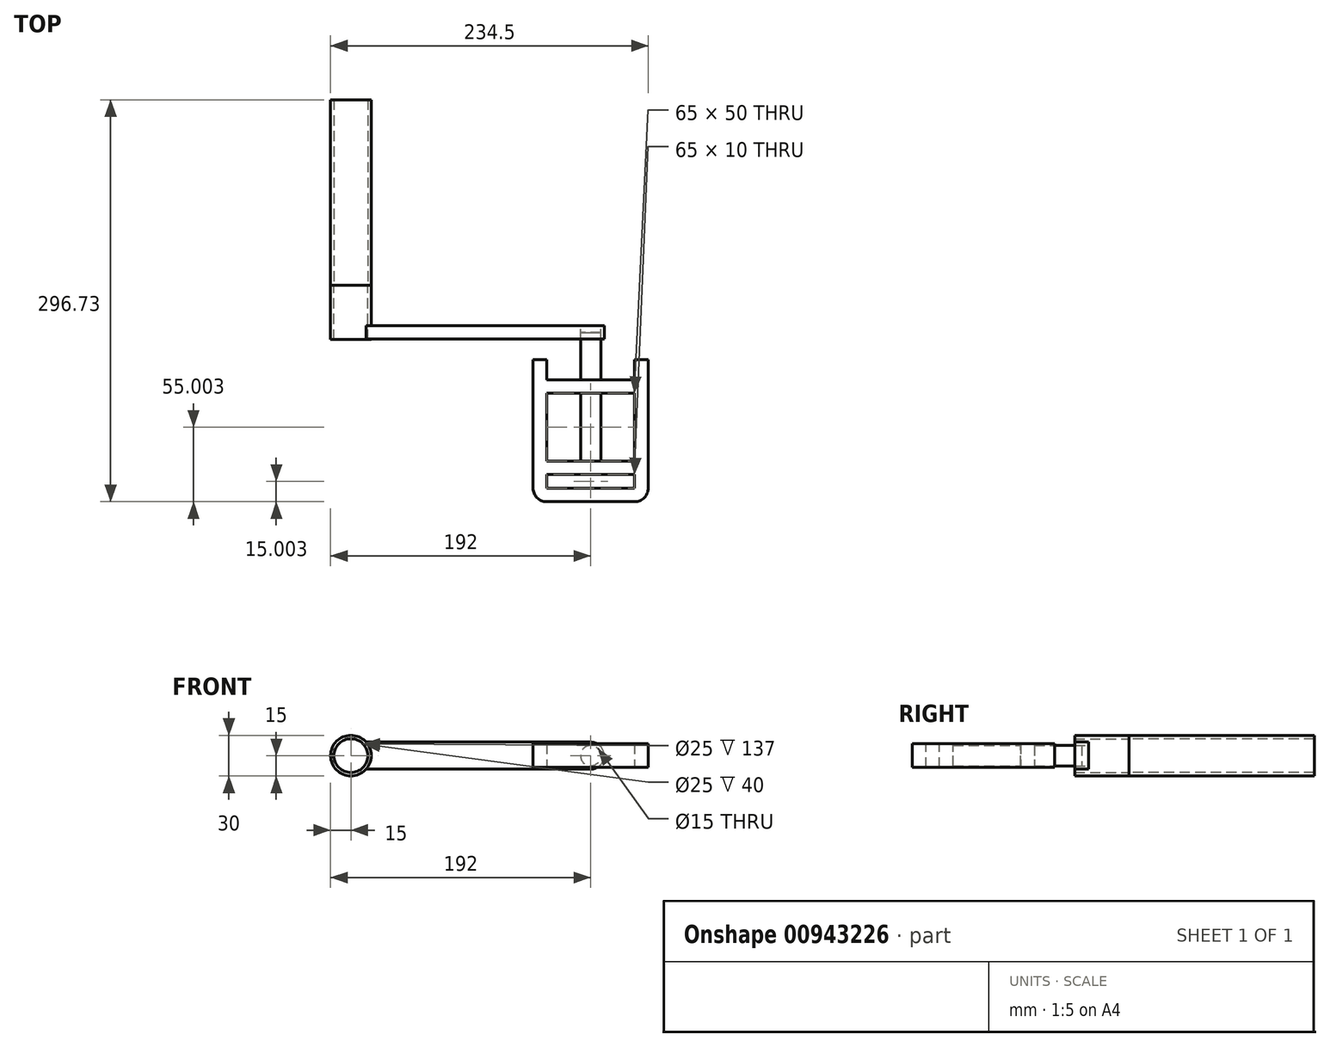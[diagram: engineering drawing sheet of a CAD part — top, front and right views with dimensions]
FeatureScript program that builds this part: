
annotation { "Feature Type Name" : "Feature", "Feature Type Description" : "" }
export const myFeature = defineFeature(function(context is Context, id is Id, definition is map)
    precondition{}
    {
        {
            var Q0;
            Q0=qCreatedBy(makeId("Front.planeOp"),FACE);
            var sketch = newSketch(context, id + "F0", { "sketchPlane" : qUnion([Q0])});
            skCircle(sketch, "E0", {"center": v(0, 0) * mm, "radius": 15 * mm});
            skCircle(sketch, "E1", {"center": v(0, 0) * mm, "radius": 12.5 * mm});
            skSolve(sketch);
        }
        {
            var Q0;
            Q0=makeQuery(id+"F0.imprint","IMPRINT",FACE,{"disambiguationData":[TD([[makeQuery(id+"F0.imprint","IMPRINT",EDGE,{"derivedFrom":sQuery(id+"F0.wireOp",EDGE,"E0")}),1.0]])]});
            extrude(context, id + "F1", {"entities" : qUnion([Q0]), "depth" : 40 * mm, "offsetDistance" : 25 * mm});
        }
        {
            var Q0;
            Q0=makeQuery(id+"F1.opExtrude","CAP_FACE",FACE,{"disambiguationData":[OSD([sQuery(id+"F0.wireOp",EDGE,"E0"),sQuery(id+"F0.wireOp",EDGE,"E1")])],"isStart":false});
            var sketch = newSketch(context, id + "F2", { "sketchPlane" : qUnion([Q0])});
            skLineSegment(sketch, "E2", {"start": v(0, 15) * mm, "end": v(0, -15) * mm});
            skSolve(sketch);
        }
        {
            var Q0;
            Q0=qCreatedBy(makeId("Right.planeOp"),FACE);
            var sketch = newSketch(context, id + "F3", { "sketchPlane" : qUnion([Q0])});
            skLineSegment(sketch, "E3", {"start": v(-39.73, 10) * mm, "end": v(-29.73, 10) * mm});
            skLineSegment(sketch, "E4.top", {"start": v(-39.73, -10) * mm, "end": v(-29.73, -10) * mm});
            skLineSegment(sketch, "E4.left", {"start": v(-39.73, 10) * mm, "end": v(-39.73, -10) * mm});
            skLineSegment(sketch, "E4.right", {"start": v(-29.73, 10) * mm, "end": v(-29.73, -10) * mm});
            skSolve(sketch);
        }
        {
            var Q0;
            Q0=qSketchRegion(id+"F3",true);
            extrude(context, id + "F4", {"entities" : qUnion([Q0]), "operationType" : NewBodyOperationType.ADD, "depth" : 177 * mm, "offsetDistance" : 25 * mm});
        }
        {
            var Q0;
            {var subQ0=sQuery(id+"F2.wireOp",EDGE,"E2");var subQ1=makeQuery(id+"F1.opExtrude","CAP_EDGE",EDGE,{"disambiguationData":[OSD([sQuery(id+"F0.wireOp",EDGE,"E1")])],"isStart":false});var subQ2=makeQuery(id+"F2.imprint","INTERSECT",VERTEX,{"disambiguationData":[OD(0.0)],"derivedFrom":[subQ1,subQ0]});Q0=makeQuery(id+"F2.imprint","IMPRINT",FACE,{"disambiguationData":[TD([[makeQuery(id+"F2.imprint","IMPRINT",EDGE,{"disambiguationData":[TD([[subQ2,-1.0]])],"derivedFrom":subQ0}),1.0]])]});}
            extrude(context, id + "F5", {"entities" : qUnion([Q0]), "operationType" : NewBodyOperationType.REMOVE, "oppositeDirection" : true, "depth" : 11 * mm, "offsetDistance" : 25 * mm});
        }
        {
            var Q0;
            {var subQ1=sQuery(id+"F3.wireOp",EDGE,"E4.right");Q0=makeQuery(id+"F4.boolean.opBoolean","SPLIT",FACE,{"disambiguationData":[TD([makeQuery(id+"F1.opExtrude","SWEPT_FACE",FACE,{"disambiguationData":[OSD([sQuery(id+"F0.wireOp",EDGE,"E0")])]})])],"derivedFrom":makeQuery(id+"F4.opExtrude","SWEPT_FACE",FACE,{"disambiguationData":[OSD([subQ1])]})});}
            var sketch = newSketch(context, id + "F6", { "sketchPlane" : qUnion([Q0])});
            skCircle(sketch, "E5", {"center": v(-177, 0) * mm, "radius": 10 * mm});
            skCircle(sketch, "E6", {"center": v(-177, 0) * mm, "radius": 7.5 * mm});
            skSolve(sketch);
        }
        {
            var Q0;
            {var subQ0=sQuery(id+"F6.wireOp",EDGE,"E6");var subQ1=makeQuery(id+"F4.opExtrude","CAP_EDGE",EDGE,{"disambiguationData":[OSD([sQuery(id+"F3.wireOp",EDGE,"E4.right")])],"isStart":false});var subQ2=makeQuery(id+"F6.imprint","INTERSECT",VERTEX,{"disambiguationData":[OD(0.0)],"derivedFrom":[subQ1,subQ0]});Q0=makeQuery(id+"F6.imprint","IMPRINT",FACE,{"disambiguationData":[TD([[makeQuery(id+"F6.imprint","IMPRINT",EDGE,{"disambiguationData":[TD([[subQ2,1.0]])],"derivedFrom":subQ0}),1.0]])]});}
            extrude(context, id + "F7", {"entities" : qUnion([Q0]), "operationType" : NewBodyOperationType.REMOVE, "oppositeDirection" : true, "depth" : 10 * mm, "offsetDistance" : 25 * mm});
        }
        {
            var Q0;
            Q0=qSketchRegion(id+"F6",true);
            extrude(context, id + "F8", {"entities" : qUnion([Q0]), "operationType" : NewBodyOperationType.ADD, "depth" : -10 * mm, "offsetDistance" : 25 * mm});
        }
        {
            var Q0;
            {var subQ1=sQuery(id+"F3.wireOp",EDGE,"E4.left");Q0=makeQuery(id+"F8.boolean.opBoolean","MERGE",FACE,{"derivedFrom":[makeQuery(id+"F4.boolean.opBoolean","SPLIT",FACE,{"disambiguationData":[TD([makeQuery(id+"F1.opExtrude","SWEPT_FACE",FACE,{"disambiguationData":[OSD([sQuery(id+"F0.wireOp",EDGE,"E0")])]})])],"derivedFrom":makeQuery(id+"F4.opExtrude","SWEPT_FACE",FACE,{"disambiguationData":[OSD([subQ1])]})}),makeQuery(id+"F8.opExtrude","CAP_FACE",FACE,{"disambiguationData":[OSD([sQuery(id+"F6.wireOp",EDGE,"E5"),sQuery(id+"F6.wireOp",EDGE,"E6")])],"isStart":false})]});}
            var sketch = newSketch(context, id + "F9", { "sketchPlane" : qUnion([Q0])});
            skCircle(sketch, "E7", {"center": v(177, 0) * mm, "radius": 7.5 * mm});
            skSolve(sketch);
        }
        {
            var Q0;
            Q0=makeQuery(id+"F9.imprint","IMPRINT",FACE,{"disambiguationData":[TD([[makeQuery(id+"F9.imprint","IMPRINT",EDGE,{"derivedFrom":sQuery(id+"F9.wireOp",EDGE,"E7")}),-1.0]])]});
            extrude(context, id + "F10", {"entities" : qUnion([Q0]), "depth" : 30 * mm, "offsetDistance" : 25 * mm, "hasSecondDirection" : true, "secondDirectionOppositeDirection" : true, "secondDirectionDepth" : 5 * mm});
        }
        {
            var Q0;
            Q0=makeQuery(id+"F10.opExtrude","CAP_FACE",FACE,{"disambiguationData":[OSD([sQuery(id+"F9.wireOp",EDGE,"E7")])],"isStart":false});
            var sketch = newSketch(context, id + "F11", { "sketchPlane" : qUnion([Q0])});
            skLineSegment(sketch, "E8.bottom", {"start": v(209.5, 8.75) * mm, "end": v(144.5, 8.75) * mm});
            skLineSegment(sketch, "E8.top", {"start": v(209.5, -8.75) * mm, "end": v(144.5, -8.75) * mm});
            skLineSegment(sketch, "E8.left", {"start": v(209.5, 8.75) * mm, "end": v(209.5, -8.75) * mm});
            skLineSegment(sketch, "E8.right", {"start": v(144.5, 8.75) * mm, "end": v(144.5, -8.75) * mm});
            skPoint(sketch, "E8.middle", {"position": v(177, 0) * mm});
            skSolve(sketch);
        }
        {
            var Q0;
            Q0=makeQuery(id+"F11.imprint","IMPRINT",FACE,{"disambiguationData":[TD([[makeQuery(id+"F11.imprint","IMPRINT",EDGE,{"derivedFrom":makeQuery(id+"F10.opExtrude","CAP_EDGE",EDGE,{"disambiguationData":[OSD([sQuery(id+"F9.wireOp",EDGE,"E7")])],"isStart":false})}),-1.0]])]});
            var Q1;
            Q1=makeQuery(id+"F11.imprint","IMPRINT",FACE,{"disambiguationData":[TD([[makeQuery(id+"F11.imprint","IMPRINT",EDGE,{"derivedFrom":sQuery(id+"F11.wireOp",EDGE,"E8.bottom")}),1.0]])]});
            extrude(context, id + "F12", {"entities" : qUnion([Q0, Q1]), "operationType" : NewBodyOperationType.ADD, "depth" : 10 * mm, "offsetDistance" : 25 * mm});
        }
        {
            var Q0;
            Q0=makeQuery(id+"F12.opExtrude","CAP_FACE",FACE,{"disambiguationData":[OSD([sQuery(id+"F11.wireOp",EDGE,"E8.bottom"),sQuery(id+"F11.wireOp",EDGE,"E8.top"),sQuery(id+"F11.wireOp",EDGE,"E8.left"),sQuery(id+"F11.wireOp",EDGE,"E8.right")])],"isStart":false});
            var sketch = newSketch(context, id + "F13", { "sketchPlane" : qUnion([Q0])});
            skCircle(sketch, "E9", {"center": v(177, 0) * mm, "radius": 7.5 * mm});
            skSolve(sketch);
        }
        {
            var Q0;
            Q0=makeQuery(id+"F13.imprint","IMPRINT",FACE,{"disambiguationData":[TD([[makeQuery(id+"F13.imprint","IMPRINT",EDGE,{"derivedFrom":sQuery(id+"F13.wireOp",EDGE,"E9")}),1.0]])]});
            extrude(context, id + "F14", {"entities" : qUnion([Q0]), "operationType" : NewBodyOperationType.ADD, "depth" : 50 * mm, "offsetDistance" : 25 * mm});
        }
        {
            var Q0;
            Q0=makeQuery(id+"F14.opExtrude","CAP_FACE",FACE,{"disambiguationData":[OSD([sQuery(id+"F13.wireOp",EDGE,"E9")])],"isStart":false});
            var sketch = newSketch(context, id + "F15", { "sketchPlane" : qUnion([Q0])});
            skLineSegment(sketch, "E10.bottom", {"start": v(209.5, -8.75) * mm, "end": v(144.5, -8.75) * mm});
            skLineSegment(sketch, "E10.top", {"start": v(209.5, 8.75) * mm, "end": v(144.5, 8.75) * mm});
            skLineSegment(sketch, "E10.left", {"start": v(209.5, -8.75) * mm, "end": v(209.5, 8.75) * mm});
            skLineSegment(sketch, "E10.right", {"start": v(144.5, -8.75) * mm, "end": v(144.5, 8.75) * mm});
            skPoint(sketch, "E10.middle", {"position": v(177, 0) * mm});
            skSolve(sketch);
        }
        {
            var Q0;
            Q0=makeQuery(id+"F15.imprint","IMPRINT",FACE,{"disambiguationData":[TD([[makeQuery(id+"F15.imprint","IMPRINT",EDGE,{"derivedFrom":sQuery(id+"F15.wireOp",EDGE,"E10.bottom")}),-1.0]])]});
            var Q1;
            Q1=makeQuery(id+"F15.imprint","IMPRINT",FACE,{"disambiguationData":[TD([[makeQuery(id+"F15.imprint","IMPRINT",EDGE,{"derivedFrom":makeQuery(id+"F14.opExtrude","CAP_EDGE",EDGE,{"disambiguationData":[OSD([sQuery(id+"F13.wireOp",EDGE,"E9")])],"isStart":false})}),1.0]])]});
            extrude(context, id + "F16", {"entities" : qUnion([Q0, Q1]), "operationType" : NewBodyOperationType.ADD, "depth" : 10 * mm, "offsetDistance" : 25 * mm});
        }
        {
            var Q0;
            Q0=makeQuery(id+"F12.opExtrude","SWEPT_FACE",FACE,{"disambiguationData":[OSD([sQuery(id+"F11.wireOp",EDGE,"E8.bottom")])]});
            var sketch = newSketch(context, id + "F17", { "sketchPlane" : qUnion([Q0])});
            skLineSegment(sketch, "E11.bottom", {"start": v(144.5, -69.73) * mm, "end": v(134.5, -69.73) * mm});
            skLineSegment(sketch, "E11.top", {"start": v(144.5, -149.73) * mm, "end": v(134.5, -149.73) * mm});
            skLineSegment(sketch, "E11.left", {"start": v(144.5, -69.73) * mm, "end": v(144.5, -149.73) * mm});
            skLineSegment(sketch, "E11.right", {"start": v(134.5, -69.73) * mm, "end": v(134.5, -149.73) * mm});
            skArc(sketch, "E12", {"start": v(134.5, -149.73) * mm, "mid": v(137.43, -156.8) * mm, "end": v(144.5, -159.73) * mm});
            skLineSegment(sketch, "E13.bottom", {"start": v(144.5, -149.73) * mm, "end": v(209.5, -149.73) * mm});
            skLineSegment(sketch, "E13.top", {"start": v(144.5, -159.73) * mm, "end": v(209.5, -159.73) * mm});
            skLineSegment(sketch, "E13.left", {"start": v(144.5, -149.73) * mm, "end": v(144.5, -159.73) * mm});
            skLineSegment(sketch, "E13.right", {"start": v(209.5, -149.73) * mm, "end": v(209.5, -159.73) * mm});
            skArc(sketch, "E14", {"start": v(209.5, -159.73) * mm, "mid": v(216.57, -156.8) * mm, "end": v(219.5, -149.73) * mm});
            skLineSegment(sketch, "E15.bottom", {"start": v(209.5, -149.73) * mm, "end": v(219.5, -149.73) * mm});
            skLineSegment(sketch, "E15.top", {"start": v(209.5, -69.73) * mm, "end": v(219.5, -69.73) * mm});
            skLineSegment(sketch, "E15.left", {"start": v(209.5, -149.73) * mm, "end": v(209.5, -69.73) * mm});
            skLineSegment(sketch, "E15.right", {"start": v(219.5, -149.73) * mm, "end": v(219.5, -69.73) * mm});
            skLineSegment(sketch, "E16.top", {"start": v(144.5, -54.73) * mm, "end": v(134.5, -54.73) * mm});
            skLineSegment(sketch, "E16.left", {"start": v(144.5, -69.73) * mm, "end": v(144.5, -54.73) * mm});
            skLineSegment(sketch, "E16.right", {"start": v(134.5, -69.73) * mm, "end": v(134.5, -54.73) * mm});
            skLineSegment(sketch, "E17.top", {"start": v(209.5, -54.73) * mm, "end": v(219.5, -54.73) * mm});
            skLineSegment(sketch, "E17.left", {"start": v(209.5, -69.73) * mm, "end": v(209.5, -54.73) * mm});
            skLineSegment(sketch, "E17.right", {"start": v(219.5, -69.73) * mm, "end": v(219.5, -54.73) * mm});
            skSolve(sketch);
        }
        {
            var Q0;
            Q0=makeQuery(id+"F17.imprint","IMPRINT",FACE,{"disambiguationData":[TD([[makeQuery(id+"F17.imprint","IMPRINT",EDGE,{"derivedFrom":sQuery(id+"F17.wireOp",EDGE,"E15.top")}),1.0]])]});
            var Q1;
            {var subQ4=sQuery(id+"F17.wireOp",EDGE,"E15.bottom");Q1=makeQuery(id+"F17.imprint","IMPRINT",FACE,{"disambiguationData":[TD([[makeQuery(id+"F17.imprint","IMPRINT",EDGE,{"derivedFrom":subQ4}),1.0]])]});}
            var Q2;
            Q2=makeQuery(id+"F17.imprint","IMPRINT",FACE,{"disambiguationData":[TD([[makeQuery(id+"F17.imprint","IMPRINT",EDGE,{"derivedFrom":sQuery(id+"F17.wireOp",EDGE,"E13.right")}),1.0]])]});
            var Q3;
            Q3=makeQuery(id+"F17.imprint","IMPRINT",FACE,{"disambiguationData":[TD([[makeQuery(id+"F17.imprint","IMPRINT",EDGE,{"derivedFrom":sQuery(id+"F17.wireOp",EDGE,"E13.bottom")}),-1.0]])]});
            var Q4;
            Q4=makeQuery(id+"F17.imprint","IMPRINT",FACE,{"disambiguationData":[TD([[makeQuery(id+"F17.imprint","IMPRINT",EDGE,{"derivedFrom":sQuery(id+"F17.wireOp",EDGE,"E11.top")}),1.0]])]});
            var Q5;
            {var subQ4=sQuery(id+"F17.wireOp",EDGE,"E11.top");Q5=makeQuery(id+"F17.imprint","IMPRINT",FACE,{"disambiguationData":[TD([[makeQuery(id+"F17.imprint","IMPRINT",EDGE,{"derivedFrom":subQ4}),-1.0]])]});}
            var Q6;
            Q6=makeQuery(id+"F17.imprint","IMPRINT",FACE,{"disambiguationData":[TD([[makeQuery(id+"F17.imprint","IMPRINT",EDGE,{"derivedFrom":sQuery(id+"F17.wireOp",EDGE,"E11.bottom")}),-1.0]])]});
            extrude(context, id + "F18", {"entities" : qUnion([Q0, Q1, Q2, Q3, Q4, Q5, Q6]), "operationType" : NewBodyOperationType.ADD, "depth" : -17.5 * mm, "offsetDistance" : 25 * mm});
        }
        {
            var Q0;
            Q0=makeQuery(id+"F1.opExtrude","CAP_FACE",FACE,{"disambiguationData":[OSD([sQuery(id+"F0.wireOp",EDGE,"E0"),sQuery(id+"F0.wireOp",EDGE,"E1")])],"isStart":true});
            var sketch = newSketch(context, id + "F19", { "sketchPlane" : qUnion([Q0])});
            skCircle(sketch, "E18", {"center": v(0, 0) * mm, "radius": 12.5 * mm});
            skCircle(sketch, "E19", {"center": v(0, 0) * mm, "radius": 15 * mm});
            skSolve(sketch);
        }
        {
            var Q0;
            Q0=qSketchRegion(id+"F19",true);
            extrude(context, id + "F20", {"entities" : qUnion([Q0]), "depth" : 137 * mm, "offsetDistance" : 25 * mm});
        }
    });
